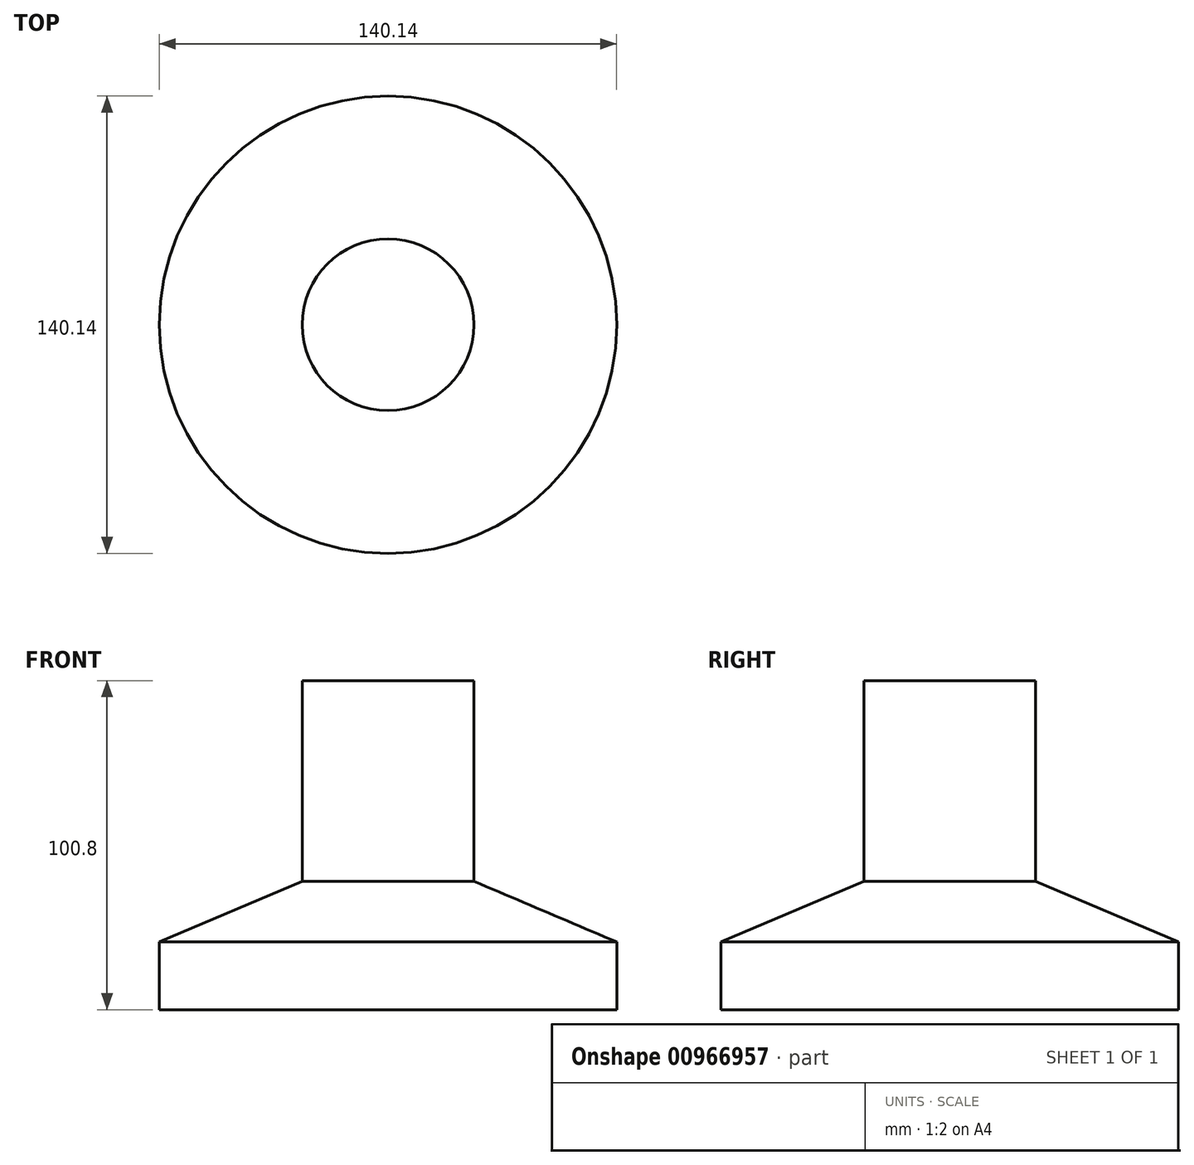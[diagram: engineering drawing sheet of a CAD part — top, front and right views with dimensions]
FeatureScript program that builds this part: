
annotation { "Feature Type Name" : "Feature", "Feature Type Description" : "" }
export const myFeature = defineFeature(function(context is Context, id is Id, definition is map)
    precondition{}
    {
        {
            var Q0;
            Q0=qCreatedBy(makeId("Front.planeOp"),FACE);
            var sketch = newSketch(context, id + "F0", { "sketchPlane" : qUnion([Q0])});
            skLineSegment(sketch, "E0", {"start": v(0, 0) * mm, "end": v(-70.07, 0) * mm});
            skLineSegment(sketch, "E1", {"start": v(-70.07, 0) * mm, "end": v(-70.07, 20.72) * mm});
            skLineSegment(sketch, "E2", {"start": v(-70.07, 20.72) * mm, "end": v(-26.3, 39.34) * mm});
            skLineSegment(sketch, "E3", {"start": v(-26.3, 39.34) * mm, "end": v(-26.3, 100.8) * mm});
            skLineSegment(sketch, "E4", {"start": v(-26.3, 100.8) * mm, "end": v(0, 100.8) * mm});
            skLineSegment(sketch, "E5", {"start": v(0, 100.8) * mm, "end": v(0, 0) * mm});
            skSolve(sketch);
        }
        {
            var Q0;
            Q0 = qSketchRegion(id + "F0", true);
            var Q1;
            Q1=sQuery(id+"F0.wireOp",EDGE,"E5");
            revolve(context, id + "F1", {"surfaceOperationType" : NewSurfaceOperationType.NEW, "entities" : qUnion([Q0]), "axis" : qUnion([Q1]), "revolveType" : RevolveType.FULL});
        }
    });
